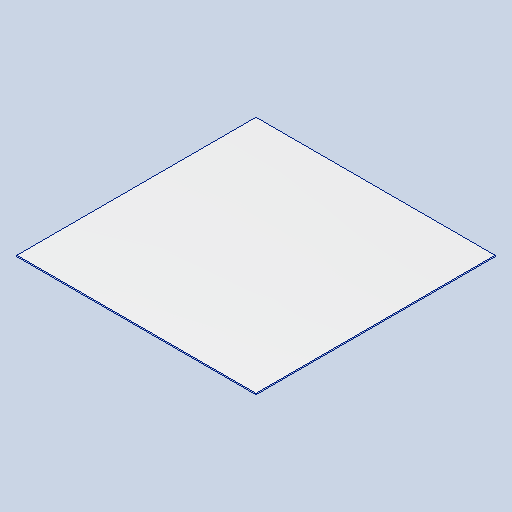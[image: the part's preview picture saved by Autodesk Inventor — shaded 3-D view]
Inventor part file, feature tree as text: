
AUTODESK INVENTOR PART (.ipt)
format: ipt  version: 2022 (Build 260153000, 153)  size: 94,208 bytes
history: native  units: in
note: dims shown in document units (in); Inventor stores cm internally (conversion verified against a paired STEP export)
features: extrude x1, sketch x1
ambient origin geometry x8: Origin, YZ Plane, XZ Plane, XY Plane, X Axis, Y Axis, Z Axis, Center Point
bodies: Solid1 (feature_tree)
feature tree (2):
  extrude  "Extrusion1"  Depth=12.0in
  sketch  "Sketch1"  dims[d0=12.0in d1=12.0in d2=0.0625in d3=0.0in]
